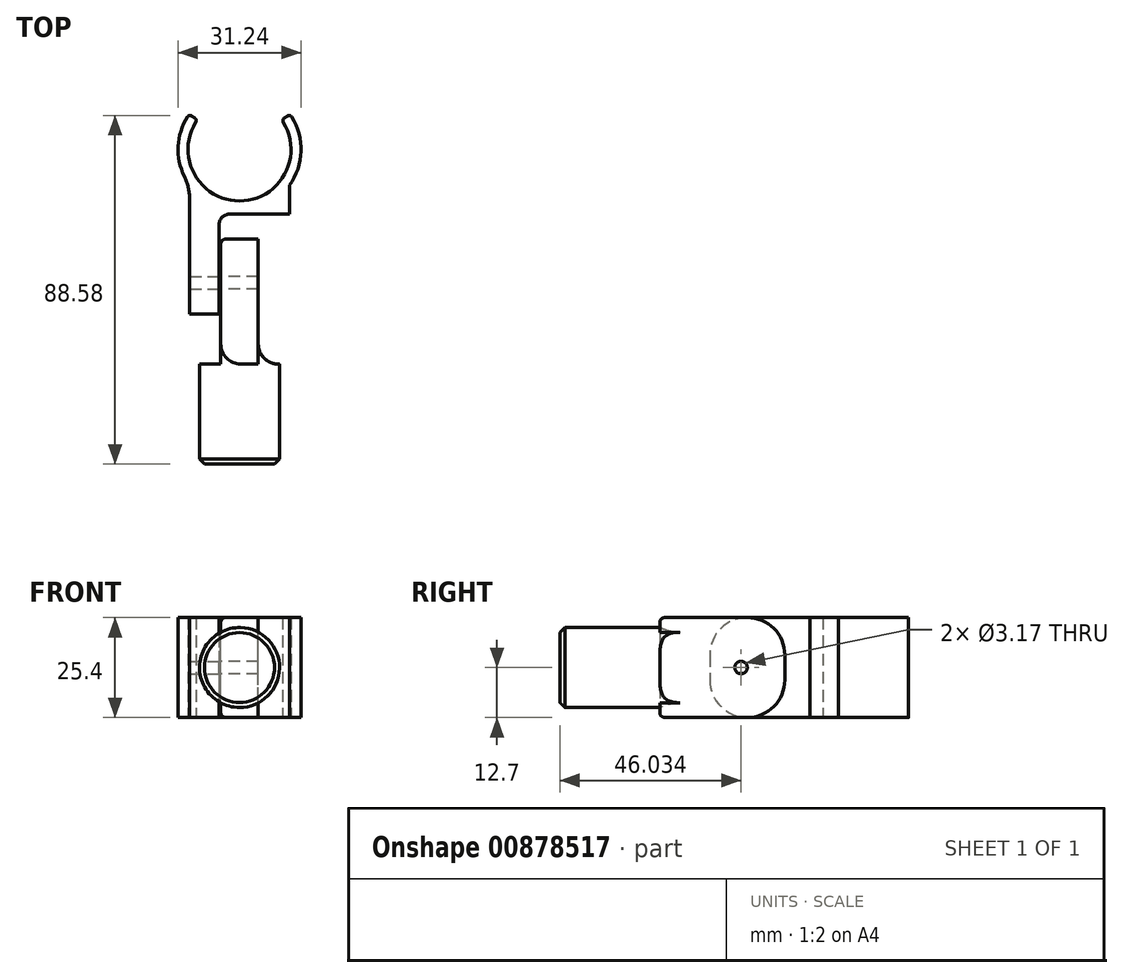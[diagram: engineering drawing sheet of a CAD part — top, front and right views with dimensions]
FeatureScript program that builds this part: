
annotation { "Feature Type Name" : "Feature", "Feature Type Description" : "" }
export const myFeature = defineFeature(function(context is Context, id is Id, definition is map)
    precondition{}
    {
        {
            var Q0;
            Q0=qCreatedBy(makeId("Top.planeOp"),FACE);
            var sketch = newSketch(context, id + "F0", { "sketchPlane" : qUnion([Q0])});
            skCircle(sketch, "E0", {"center": v(0, 0) * mm, "radius": 15.62 * mm});
            skCircle(sketch, "E1", {"center": v(0, 0) * mm, "radius": 13.08 * mm});
            skLineSegment(sketch, "E2", {"start": v(-53.94, 0) * mm, "end": v(51.47, 0) * mm, "construction": true});
            skLineSegment(sketch, "E3", {"start": v(0, 37.95) * mm, "end": v(0, -48.77) * mm, "construction": true});
            skLineSegment(sketch, "E4", {"start": v(0, 0) * mm, "end": v(-12.8, 8.96) * mm});
            skLineSegment(sketch, "E5.MirrorCS", {"start": v(0, 0) * mm, "end": v(12.8, 8.96) * mm});
            skLineSegment(sketch, "E6.top", {"start": v(-12.7, -16.43) * mm, "end": v(12.7, -16.43) * mm});
            skLineSegment(sketch, "E6.left", {"start": v(-12.7, -9.1) * mm, "end": v(-12.7, -16.43) * mm});
            skLineSegment(sketch, "E6.right", {"start": v(12.7, -9.1) * mm, "end": v(12.7, -16.43) * mm});
            skPoint(sketch, "E6.middle", {"position": v(0, -12.76) * mm});
            skCircle(sketch, "E7", {"center": v(0, 0) * mm, "radius": 13.34 * mm, "construction": true});
            skLineSegment(sketch, "E8.bottom", {"start": v(12.7, -16.43) * mm, "end": v(5.14, -16.43) * mm});
            skLineSegment(sketch, "E8.top", {"start": v(12.7, -41.83) * mm, "end": v(5.14, -41.83) * mm});
            skLineSegment(sketch, "E8.left", {"start": v(12.7, -16.43) * mm, "end": v(12.7, -41.83) * mm});
            skLineSegment(sketch, "E8.right", {"start": v(5.14, -16.43) * mm, "end": v(5.14, -41.83) * mm});
            skLineSegment(sketch, "E9.MirrorCS", {"start": v(-5.14, -16.43) * mm, "end": v(-5.14, -41.83) * mm});
            skLineSegment(sketch, "E10.MirrorCS", {"start": v(-12.7, -41.83) * mm, "end": v(-5.14, -41.83) * mm});
            skLineSegment(sketch, "E11.MirrorCS", {"start": v(-12.7, -16.43) * mm, "end": v(-12.7, -41.83) * mm});
            skSolve(sketch);
        }
        {
            var Q0;
            {var subQ0=sQuery(id+"F0.wireOp",EDGE,"E4");var subQ5=sQuery(id+"F0.wireOp",EDGE,"E0");var subQ9=makeQuery(id+"F0.imprint","INTERSECT",VERTEX,{"derivedFrom":[subQ5,subQ0]});Q0=makeQuery(id+"F0.imprint","IMPRINT",FACE,{"disambiguationData":[TD([[makeQuery(id+"F0.imprint","IMPRINT",EDGE,{"disambiguationData":[TD([[subQ9,-1.0]])],"derivedFrom":subQ5}),1.0]])]});}
            extrude(context, id + "F1", {"entities" : qUnion([Q0]), "endBound" : BoundingType.SYMMETRIC, "depth" : 25.4 * mm, "offsetDistance" : 25.4 * mm});
        }
        {
            var Q0;
            Q0=makeQuery(id+"F0.imprint","IMPRINT",FACE,{"disambiguationData":[TD([[makeQuery(id+"F0.imprint","IMPRINT",EDGE,{"derivedFrom":sQuery(id+"F0.wireOp",EDGE,"E6.top")}),1.0]])]});
            var Q1;
            {var subQ0=sQuery(id+"F0.wireOp",EDGE,"E9.MirrorCS");Q1=makeQuery(id+"F0.imprint","IMPRINT",FACE,{"disambiguationData":[TD([[makeQuery(id+"F0.imprint","IMPRINT",EDGE,{"derivedFrom":subQ0}),-1.0]])]});}
            var Q2;
            Q2=makeQuery(id+"F0.imprint","IMPRINT",FACE,{"disambiguationData":[TD([[makeQuery(id+"F0.imprint","IMPRINT",EDGE,{"derivedFrom":sQuery(id+"F0.wireOp",EDGE,"E8.bottom")}),1.0]])]});
            extrude(context, id + "F2", {"entities" : qUnion([Q0, Q1, Q2]), "operationType" : NewBodyOperationType.ADD, "endBound" : BoundingType.SYMMETRIC, "depth" : 25.4 * mm, "offsetDistance" : 25.4 * mm});
        }
        {
            var Q0;
            Q0=makeQuery(id+"F2.opExtrude","SWEPT_EDGE",EDGE,{"disambiguationData":[OSD([sQuery(id+"F0.wireOp",EDGE,"E0"),sQuery(id+"F0.wireOp",EDGE,"E6.left")])]});
            var Q1;
            Q1=makeQuery(id+"F2.opExtrude","SWEPT_EDGE",EDGE,{"disambiguationData":[OSD([sQuery(id+"F0.wireOp",EDGE,"E0"),sQuery(id+"F0.wireOp",EDGE,"E6.right")])]});
            fillet(context, id + "F3", {"entities" : qUnion([Q0, Q1]), "radius" : 12.7 * mm, "tangentPropagation" : true, "allowEdgeOverflow" : false});
        }
        {
            var Q0;
            Q0=makeQuery(id+"F1.opExtrude","SWEPT_EDGE",EDGE,{"disambiguationData":[OSD([sQuery(id+"F0.wireOp",EDGE,"E0"),sQuery(id+"F0.wireOp",EDGE,"E4")])]});
            var Q1;
            Q1=makeQuery(id+"F1.opExtrude","SWEPT_EDGE",EDGE,{"disambiguationData":[OSD([sQuery(id+"F0.wireOp",EDGE,"E1"),sQuery(id+"F0.wireOp",EDGE,"E4")])]});
            var Q2;
            Q2=makeQuery(id+"F1.opExtrude","SWEPT_EDGE",EDGE,{"disambiguationData":[OSD([sQuery(id+"F0.wireOp",EDGE,"E0"),sQuery(id+"F0.wireOp",EDGE,"E5.MirrorCS")])]});
            var Q3;
            Q3=makeQuery(id+"F1.opExtrude","SWEPT_EDGE",EDGE,{"disambiguationData":[OSD([sQuery(id+"F0.wireOp",EDGE,"E1"),sQuery(id+"F0.wireOp",EDGE,"E5.MirrorCS")])]});
            fillet(context, id + "F4", {"entities" : qUnion([Q0, Q1, Q2, Q3]), "radius" : 0.76 * mm, "tangentPropagation" : true, "allowEdgeOverflow" : false});
        }
        {
            var Q0;
            Q0=qCreatedBy(makeId("Right.planeOp"),FACE);
            var sketch = newSketch(context, id + "F5", { "sketchPlane" : qUnion([Q0])});
            skLineSegment(sketch, "E12", {"start": v(-67.73, 0) * mm, "end": v(4.38, 0) * mm, "construction": true});
            skLineSegment(sketch, "E13", {"start": v(0, 23) * mm, "end": v(0, -35.14) * mm});
            skLineSegment(sketch, "E14.1", {"start": v(-16.43, 12.7) * mm, "end": v(-16.43, -12.7) * mm});
            skCircle(sketch, "E15", {"center": v(-33.9, 0) * mm, "radius": 1.59 * mm});
            skLineSegment(sketch, "E16.bottom", {"start": v(-22.78, -12.7) * mm, "end": v(-54.53, -12.7) * mm});
            skLineSegment(sketch, "E16.top", {"start": v(-22.78, 12.7) * mm, "end": v(-54.53, 12.7) * mm});
            skLineSegment(sketch, "E16.left", {"start": v(-22.78, -12.7) * mm, "end": v(-22.78, 12.7) * mm});
            skLineSegment(sketch, "E16.right", {"start": v(-54.53, -12.7) * mm, "end": v(-54.53, 12.7) * mm});
            skPoint(sketch, "E16.middle", {"position": v(-38.66, 0) * mm});
            skSolve(sketch);
        }
        {
            var Q0;
            Q0 = qSketchRegion(id + "F5", true);
            extrude(context, id + "F6", {"entities" : qUnion([Q0]), "endBound" : BoundingType.SYMMETRIC, "depth" : 9.52 * mm, "offsetDistance" : 25.4 * mm});
        }
        {
            var Q0;
            Q0=makeQuery(id+"F5.imprint","IMPRINT",FACE,{"disambiguationData":[TD([[makeQuery(id+"F5.imprint","IMPRINT",EDGE,{"derivedFrom":sQuery(id+"F5.wireOp",EDGE,"E15")}),1.0]])]});
            extrude(context, id + "F7", {"entities" : qUnion([Q0]), "operationType" : NewBodyOperationType.REMOVE, "oppositeDirection" : true, "depth" : 25.4 * mm, "offsetDistance" : 25.4 * mm, "hasSecondDirection" : true, "secondDirectionOppositeDirection" : false, "secondDirectionDepth" : 25.4 * mm});
        }
        {
            var Q0;
            Q0=makeQuery(id+"F6.opExtrude","SWEPT_FACE",FACE,{"disambiguationData":[OSD([sQuery(id+"F5.wireOp",EDGE,"E16.right")])]});
            var sketch = newSketch(context, id + "F8", { "sketchPlane" : qUnion([Q0])});
            skCircle(sketch, "E17", {"center": v(0, 0) * mm, "radius": 10.16 * mm});
            skSolve(sketch);
        }
        {
            var Q0;
            Q0 = qSketchRegion(id + "F8", true);
            extrude(context, id + "F9", {"entities" : qUnion([Q0]), "operationType" : NewBodyOperationType.ADD, "depth" : 25.4 * mm, "offsetDistance" : 25.4 * mm});
        }
        {
            var Q0;
            Q0=makeQuery(id+"F2.opExtrude","CAP_EDGE",EDGE,{"disambiguationData":[OSD([sQuery(id+"F0.wireOp",EDGE,"E8.top")])],"isStart":true});
            var Q1;
            Q1=makeQuery(id+"F2.opExtrude","CAP_EDGE",EDGE,{"disambiguationData":[OSD([sQuery(id+"F0.wireOp",EDGE,"E10.MirrorCS")])],"isStart":true});
            var Q2;
            Q2=makeQuery(id+"F2.opExtrude","CAP_EDGE",EDGE,{"disambiguationData":[OSD([sQuery(id+"F0.wireOp",EDGE,"E8.top")])],"isStart":false});
            var Q3;
            Q3=makeQuery(id+"F6.opExtrude","SWEPT_EDGE",EDGE,{"disambiguationData":[OSD([sQuery(id+"F5.wireOp",EDGE,"E16.bottom"),sQuery(id+"F5.wireOp",EDGE,"E16.left")])]});
            var Q4;
            Q4=makeQuery(id+"F6.opExtrude","SWEPT_EDGE",EDGE,{"disambiguationData":[OSD([sQuery(id+"F5.wireOp",EDGE,"E16.top"),sQuery(id+"F5.wireOp",EDGE,"E16.left")])]});
            var Q5;
            Q5=makeQuery(id+"F2.opExtrude","CAP_EDGE",EDGE,{"disambiguationData":[OSD([sQuery(id+"F0.wireOp",EDGE,"E10.MirrorCS")])],"isStart":false});
            fillet(context, id + "F10", {"entities" : qUnion([Q0, Q1, Q2, Q3, Q4, Q5]), "tangentPropagation" : true, "radius" : 9.52 * mm, "defaultsChanged" : false, "vertexSettings" : [], "allowEdgeOverflow" : false});
        }
        {
            var Q0;
            {var subQ0=sQuery(id+"F5.wireOp",EDGE,"E16.right");Q0=makeQuery(id+"F9.boolean.opBoolean","SPLIT",EDGE,{"disambiguationData":[topologyDisambiguationEdgeConnected([makeQuery(id+"F6.opExtrude","CAP_FACE",FACE,{"disambiguationData":[OSD([sQuery(id+"F5.wireOp",EDGE,"E15"),sQuery(id+"F5.wireOp",EDGE,"E16.bottom"),sQuery(id+"F5.wireOp",EDGE,"E16.top"),sQuery(id+"F5.wireOp",EDGE,"E16.left"),subQ0])],"isStart":true}),makeQuery(id+"F9.opExtrude","CAP_FACE",FACE,{"disambiguationData":[OSD([sQuery(id+"F8.wireOp",EDGE,"E17")])],"isStart":true})])],"derivedFrom":makeQuery(id+"F6.opExtrude","CAP_EDGE",EDGE,{"disambiguationData":[OSD([subQ0])],"isStart":true})});}
            var Q1;
            {var subQ0=sQuery(id+"F5.wireOp",EDGE,"E16.right");Q1=makeQuery(id+"F9.boolean.opBoolean","SPLIT",EDGE,{"disambiguationData":[topologyDisambiguationEdgeConnected([makeQuery(id+"F6.opExtrude","CAP_FACE",FACE,{"disambiguationData":[OSD([sQuery(id+"F5.wireOp",EDGE,"E15"),sQuery(id+"F5.wireOp",EDGE,"E16.bottom"),sQuery(id+"F5.wireOp",EDGE,"E16.top"),sQuery(id+"F5.wireOp",EDGE,"E16.left"),subQ0])],"isStart":false}),makeQuery(id+"F9.opExtrude","CAP_FACE",FACE,{"disambiguationData":[OSD([sQuery(id+"F8.wireOp",EDGE,"E17")])],"isStart":true})])],"derivedFrom":makeQuery(id+"F6.opExtrude","CAP_EDGE",EDGE,{"disambiguationData":[OSD([subQ0])],"isStart":false})});}
            fillet(context, id + "F11", {"entities" : qUnion([Q0, Q1]), "tangentPropagation" : true, "radius" : 5.08 * mm, "defaultsChanged" : false, "vertexSettings" : [], "allowEdgeOverflow" : false});
        }
        {
            var Q0;
            Q0=makeQuery(id+"F6.opExtrude","SWEPT_EDGE",EDGE,{"disambiguationData":[OSD([sQuery(id+"F5.wireOp",EDGE,"E16.top"),sQuery(id+"F5.wireOp",EDGE,"E16.right")])]});
            var Q1;
            Q1=makeQuery(id+"F6.opExtrude","SWEPT_EDGE",EDGE,{"disambiguationData":[OSD([sQuery(id+"F5.wireOp",EDGE,"E16.bottom"),sQuery(id+"F5.wireOp",EDGE,"E16.right")])]});
            fillet(context, id + "F12", {"entities" : qUnion([Q0, Q1]), "tangentPropagation" : true, "radius" : 1.27 * mm, "defaultsChanged" : false, "vertexSettings" : [], "allowEdgeOverflow" : false});
        }
        {
            var Q0;
            Q0=makeQuery(id+"F2.opExtrude","SWEPT_EDGE",EDGE,{"disambiguationData":[OSD([sQuery(id+"F0.wireOp",EDGE,"E6.top"),sQuery(id+"F0.wireOp",EDGE,"E8.bottom"),sQuery(id+"F0.wireOp",EDGE,"E8.right")])]});
            var Q1;
            Q1=makeQuery(id+"F2.opExtrude","SWEPT_EDGE",EDGE,{"disambiguationData":[OSD([sQuery(id+"F0.wireOp",EDGE,"E6.top"),sQuery(id+"F0.wireOp",EDGE,"E9.MirrorCS")])]});
            fillet(context, id + "F13", {"entities" : qUnion([Q0, Q1]), "tangentPropagation" : true, "radius" : 2.54 * mm, "defaultsChanged" : false, "vertexSettings" : [], "allowEdgeOverflow" : false});
        }
        {
            var Q0;
            Q0=makeQuery(id+"F9.opExtrude","CAP_FACE",FACE,{"disambiguationData":[OSD([sQuery(id+"F8.wireOp",EDGE,"E17")])],"isStart":false});
            chamfer(context, id + "F14", {"entities" : qUnion([Q0]), "width" : 1.27 * mm, "tangentPropagation" : true});
        }
    });
